# Revit family: 506_VCE-C-_-S-ZP-0-0
name_source: partatom
category: Electrical Equipment
revit_build: Autodesk Revit 2018 (Build: 20170223_1515(x64)
units: mm (PartAtom-declared; Revit-internal decimal feet)

## family parameters
Cut with Voids When Loaded = No
Host = Face
Part Type = Equipment Switch
Room Calculation Point = No
Round Connector Dimension = Use Diameter
Shared = No

## types (3) — shared parameters
Description = Air curtain ESSENSSE, ouput series C, ambient
H = 240 mm  [stored 0.787402 ft]
MC Active Power = 1 W
MC CosPhi = 0.95
MC Number of Poles = 3
MC Voltage = 0 V
MT1 = No
MT2 = Yes
Manufacturer = 2VV
PHR = 20 mm  [stored 0.0656168 ft]
PHS = 20 mm  [stored 0.0656168 ft]
R1 = 120 mm  [stored 0.393701 ft]
SketchPlaneIDs = 10482;153b746f-b00a-47b6-946a-48530699bbd5-000028f2
SketchPlaneIDsNote = Do not delete SketchPlaneIDs Paramter.It is used to identifiy Reference Line's Sketch Plane
URL = www.2vv.cz
W2 = 216 mm
W3 = 96 mm
Y1 = 20 mm  [stored 0.0656168 ft]
magiApparentLoad = 1 VA
magiPartTypeId = 506
magiProductFamilyId = VCE-C-*-S-ZP-0-0
zero-valued in all types: Default Elevation, L2D, W2D

## per-type parameters (varying)
| type | L | L2 | L3 |
| VCE-C-100-S-ZP-0-0 | 1075 mm  [stored 3.5269 ft] | 538 mm | 488 mm |
| VCE-C-200-S-ZP-0-0 | 2077 mm | 1039 mm | 989 mm |
| VCE-C-150-S-ZP-0-0 | 1577 mm | 789 mm | 739 mm |

note: column(s) folded — value = type name in every type: MC Product Code, magiProductId

note: [stored X ft] marks values corroborated as IEEE doubles in the binary element streams (Revit-internal decimal feet)

## geometry (parser evidence)
native form markers: Blend x2, Sweep x2
no freeform markers — native parametric forms only
